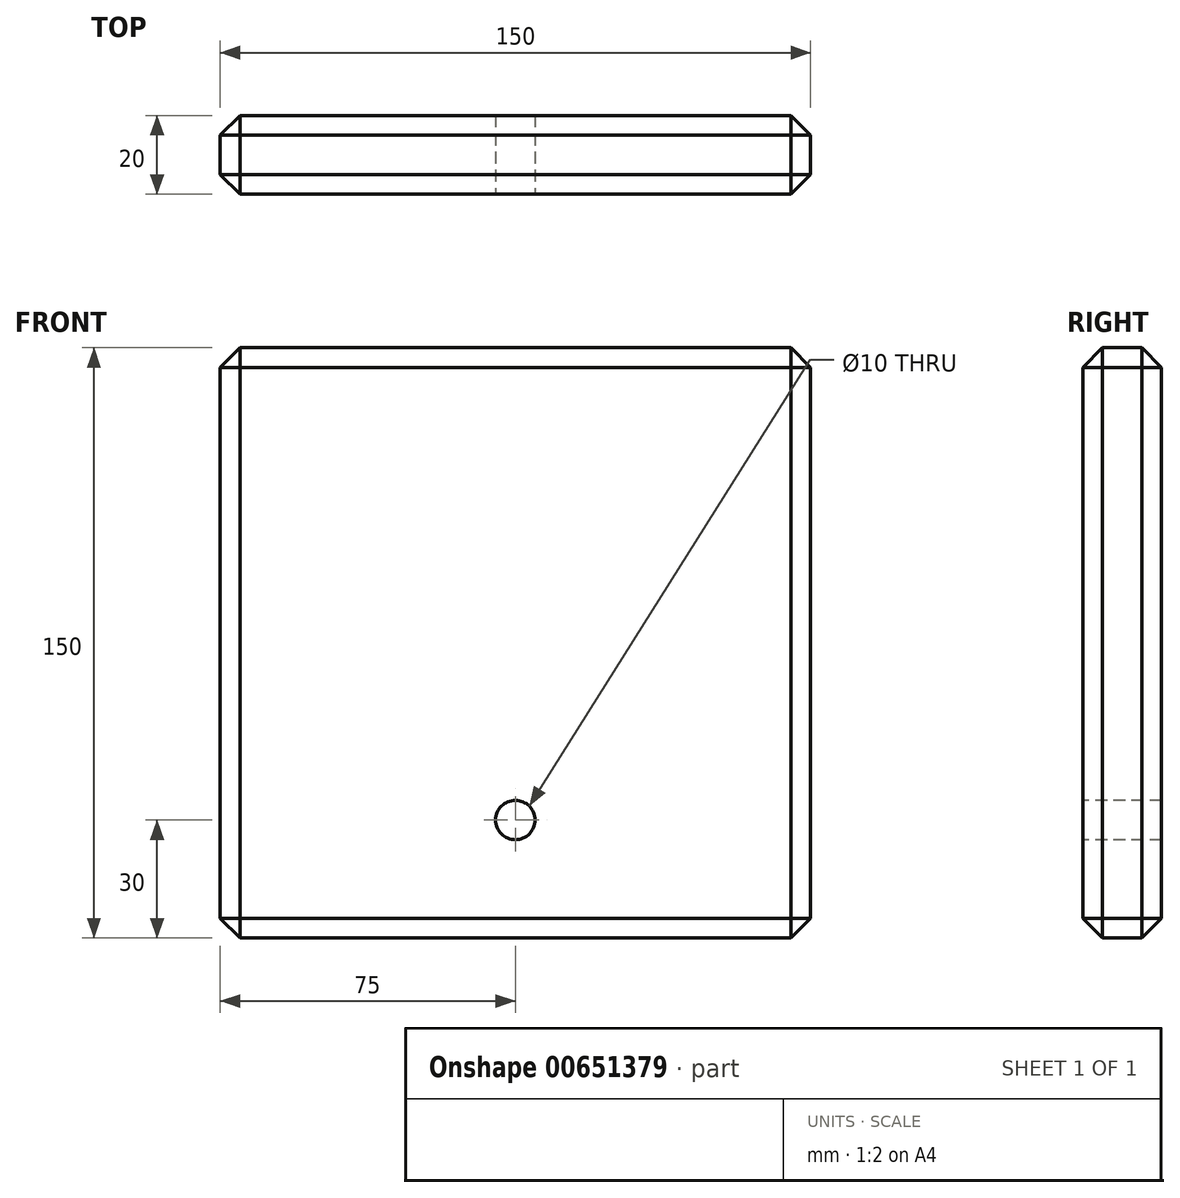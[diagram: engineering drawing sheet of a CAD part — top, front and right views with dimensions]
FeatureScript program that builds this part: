
annotation { "Feature Type Name" : "Feature", "Feature Type Description" : "" }
export const myFeature = defineFeature(function(context is Context, id is Id, definition is map)
    precondition{}
    {
        {
            var Q0;
            Q0=qCreatedBy(makeId("Front.planeOp"),FACE);
            var sketch = newSketch(context, id + "F0", { "sketchPlane" : qUnion([Q0])});
            skLineSegment(sketch, "E0.bottom", {"start": v(75, 75) * mm, "end": v(-75, 75) * mm});
            skLineSegment(sketch, "E0.top", {"start": v(75, -75) * mm, "end": v(-75, -75) * mm});
            skLineSegment(sketch, "E0.left", {"start": v(75, 75) * mm, "end": v(75, -75) * mm});
            skLineSegment(sketch, "E0.right", {"start": v(-75, 75) * mm, "end": v(-75, -75) * mm});
            skPoint(sketch, "E0.middle", {"position": v(0, 0) * mm});
            skSolve(sketch);
        }
        {
            var Q0;
            Q0=makeQuery(id+"F0.imprint","IMPRINT",FACE,{"disambiguationData":[TD([[makeQuery(id+"F0.imprint","IMPRINT",EDGE,{"derivedFrom":sQuery(id+"F0.wireOp",EDGE,"E0.bottom")}),1.0]])]});
            extrude(context, id + "F1", {"entities" : qUnion([Q0]), "depth" : 20 * mm, "offsetDistance" : 25 * mm});
        }
        {
            var Q0;
            Q0=makeQuery(id+"F1.opExtrude","CAP_FACE",FACE,{"disambiguationData":[OSD([sQuery(id+"F0.wireOp",EDGE,"E0.bottom"),sQuery(id+"F0.wireOp",EDGE,"E0.top"),sQuery(id+"F0.wireOp",EDGE,"E0.left"),sQuery(id+"F0.wireOp",EDGE,"E0.right")])],"isStart":false});
            var sketch = newSketch(context, id + "F2", { "sketchPlane" : qUnion([Q0])});
            skCircle(sketch, "E1", {"center": v(0, -45) * mm, "radius": 5 * mm});
            skSolve(sketch);
        }
        {
            var Q0;
            Q0 = qSketchRegion(id + "F2", true);
            extrude(context, id + "F3", {"entities" : qUnion([Q0]), "operationType" : NewBodyOperationType.REMOVE, "endBound" : BoundingType.THROUGH_ALL, "oppositeDirection" : true, "depth" : 25 * mm, "offsetDistance" : 25 * mm});
        }
        {
            var Q0;
            Q0=makeQuery(id+"F1.opExtrude","SWEPT_FACE",FACE,{"disambiguationData":[OSD([sQuery(id+"F0.wireOp",EDGE,"E0.bottom")])]});
            var Q1;
            Q1=makeQuery(id+"F1.opExtrude","SWEPT_FACE",FACE,{"disambiguationData":[OSD([sQuery(id+"F0.wireOp",EDGE,"E0.left")])]});
            var Q2;
            Q2=makeQuery(id+"F1.opExtrude","SWEPT_FACE",FACE,{"disambiguationData":[OSD([sQuery(id+"F0.wireOp",EDGE,"E0.top")])]});
            var Q3;
            Q3=makeQuery(id+"F1.opExtrude","SWEPT_FACE",FACE,{"disambiguationData":[OSD([sQuery(id+"F0.wireOp",EDGE,"E0.right")])]});
            chamfer(context, id + "F4", {"entities" : qUnion([Q0, Q1, Q2, Q3]), "width" : 5 * mm, "tangentPropagation" : true});
        }
    });
